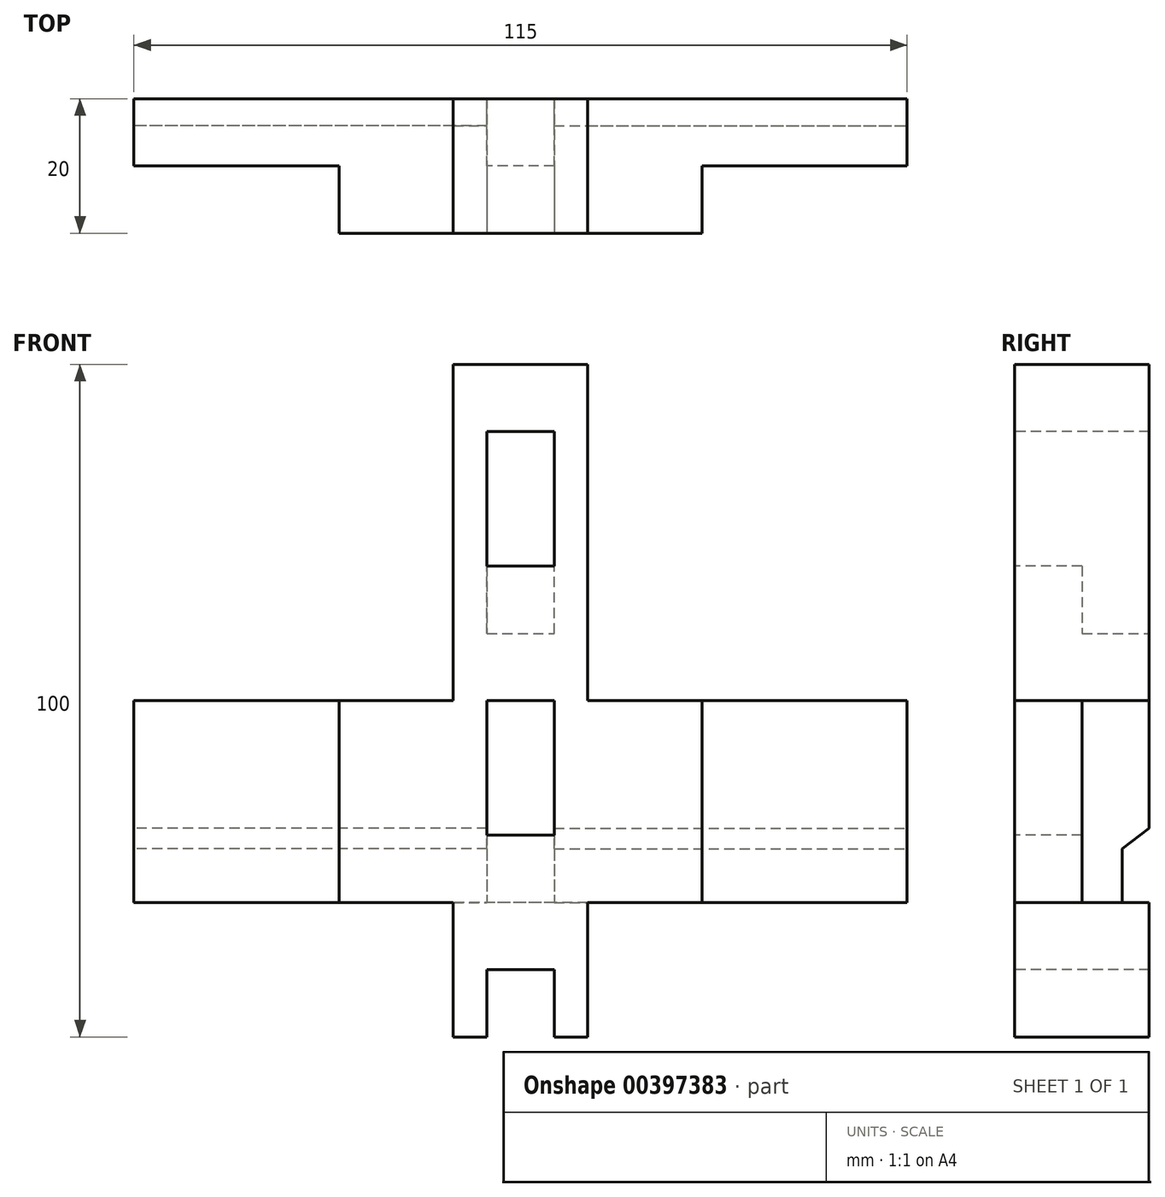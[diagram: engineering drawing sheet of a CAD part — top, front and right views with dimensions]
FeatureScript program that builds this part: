
annotation { "Feature Type Name" : "Feature", "Feature Type Description" : "" }
export const myFeature = defineFeature(function(context is Context, id is Id, definition is map)
    precondition{}
    {
        {
            var Q0;
            Q0=qCreatedBy(makeId("Front.planeOp"),FACE);
            var sketch = newSketch(context, id + "F0", { "sketchPlane" : qUnion([Q0])});
            skLineSegment(sketch, "E0", {"start": v(0, 0) * mm, "end": v(0, 100) * mm});
            skLineSegment(sketch, "E1", {"start": v(0, 100) * mm, "end": v(-10, 100) * mm});
            skLineSegment(sketch, "E2", {"start": v(-10, 100) * mm, "end": v(-10, 50) * mm});
            skLineSegment(sketch, "E3", {"start": v(-10, 50) * mm, "end": v(-57.5, 50) * mm});
            skLineSegment(sketch, "E4", {"start": v(-57.5, 50) * mm, "end": v(-57.5, 20) * mm});
            skLineSegment(sketch, "E5", {"start": v(-57.5, 20) * mm, "end": v(-10, 20) * mm});
            skLineSegment(sketch, "E6", {"start": v(-10, 20) * mm, "end": v(-10, 0) * mm});
            skLineSegment(sketch, "E7", {"start": v(-10, 0) * mm, "end": v(0, 0) * mm});
            skLineSegment(sketch, "E8.MirrorCS", {"start": v(10, 100) * mm, "end": v(10, 50) * mm});
            skLineSegment(sketch, "E9.MirrorCS", {"start": v(57.5, 50) * mm, "end": v(57.5, 20) * mm});
            skLineSegment(sketch, "E10.MirrorCS", {"start": v(57.5, 20) * mm, "end": v(10, 20) * mm});
            skLineSegment(sketch, "E11.MirrorCS", {"start": v(0, 100) * mm, "end": v(10, 100) * mm});
            skLineSegment(sketch, "E12.MirrorCS", {"start": v(10, 50) * mm, "end": v(57.5, 50) * mm});
            skLineSegment(sketch, "E13.MirrorCS", {"start": v(10, 20) * mm, "end": v(10, 0) * mm});
            skLineSegment(sketch, "E14.MirrorCS", {"start": v(10, 0) * mm, "end": v(0, 0) * mm});
            skSolve(sketch);
        }
        {
            var Q0;
            Q0 = qSketchRegion(id + "F0", true);
            extrude(context, id + "F1", {"entities" : qUnion([Q0]), "depth" : 20 * mm});
        }
        {
            var Q0;
            Q0=makeQuery(id+"F1.opExtrude","SWEPT_FACE",FACE,{"disambiguationData":[OSD([sQuery(id+"F0.wireOp",EDGE,"E5")])]});
            var sketch = newSketch(context, id + "F2", { "sketchPlane" : qUnion([Q0])});
            skLineSegment(sketch, "E15.bottom", {"start": v(-57.5, 20) * mm, "end": v(-27, 20) * mm});
            skLineSegment(sketch, "E15.top", {"start": v(-57.5, 10) * mm, "end": v(-27, 10) * mm});
            skLineSegment(sketch, "E15.left", {"start": v(-57.5, 20) * mm, "end": v(-57.5, 10) * mm});
            skLineSegment(sketch, "E15.right", {"start": v(-27, 20) * mm, "end": v(-27, 10) * mm});
            skSolve(sketch);
        }
        {
            var Q0;
            Q0=makeQuery(id+"F2.imprint","IMPRINT",FACE,{"disambiguationData":[TD([[makeQuery(id+"F2.imprint","IMPRINT",EDGE,{"derivedFrom":sQuery(id+"F2.wireOp",EDGE,"E15.bottom")}),-1.0]])]});
            extrude(context, id + "F3", {"entities" : qUnion([Q0]), "operationType" : NewBodyOperationType.REMOVE, "endBound" : BoundingType.UP_TO_NEXT, "oppositeDirection" : true, "depth" : 25.4 * mm});
        }
        {
            var Q0;
            Q0=makeQuery(id+"F1.opExtrude","SWEPT_FACE",FACE,{"disambiguationData":[OSD([sQuery(id+"F0.wireOp",EDGE,"E10.MirrorCS")])]});
            var sketch = newSketch(context, id + "F4", { "sketchPlane" : qUnion([Q0])});
            skLineSegment(sketch, "E16.bottom", {"start": v(57.5, 20) * mm, "end": v(27, 20) * mm});
            skLineSegment(sketch, "E16.top", {"start": v(57.5, 10) * mm, "end": v(27, 10) * mm});
            skLineSegment(sketch, "E16.left", {"start": v(57.5, 20) * mm, "end": v(57.5, 10) * mm});
            skLineSegment(sketch, "E16.right", {"start": v(27, 20) * mm, "end": v(27, 10) * mm});
            skSolve(sketch);
        }
        {
            var Q0;
            Q0=makeQuery(id+"F4.imprint","IMPRINT",FACE,{"disambiguationData":[TD([[makeQuery(id+"F4.imprint","IMPRINT",EDGE,{"derivedFrom":sQuery(id+"F4.wireOp",EDGE,"E16.bottom")}),1.0]])]});
            extrude(context, id + "F5", {"entities" : qUnion([Q0]), "operationType" : NewBodyOperationType.REMOVE, "endBound" : BoundingType.UP_TO_NEXT, "oppositeDirection" : true, "depth" : 25.4 * mm});
        }
        {
            var Q0;
            Q0=makeQuery(id+"F1.opExtrude","SWEPT_FACE",FACE,{"disambiguationData":[OSD([sQuery(id+"F0.wireOp",EDGE,"E4")])]});
            var sketch = newSketch(context, id + "F6", { "sketchPlane" : qUnion([Q0])});
            skLineSegment(sketch, "E17", {"start": v(0, 20) * mm, "end": v(4, 20) * mm});
            skLineSegment(sketch, "E18", {"start": v(4, 20) * mm, "end": v(4, 28) * mm});
            skLineSegment(sketch, "E19", {"start": v(0, 28) * mm, "end": v(0, 20) * mm});
            skLineSegment(sketch, "E20", {"start": v(0, 31) * mm, "end": v(0, 28) * mm});
            skLineSegment(sketch, "E21", {"start": v(0, 31) * mm, "end": v(4, 28) * mm});
            skSolve(sketch);
        }
        {
            var Q0;
            Q0=makeQuery(id+"F6.imprint","IMPRINT",FACE,{"disambiguationData":[TD([[makeQuery(id+"F6.imprint","IMPRINT",EDGE,{"derivedFrom":sQuery(id+"F6.wireOp",EDGE,"E17")}),-1.0]])]});
            var Q1;
            Q1=makeQuery(id+"F1.opExtrude","SWEPT_FACE",FACE,{"disambiguationData":[OSD([sQuery(id+"F0.wireOp",EDGE,"E6")])]});
            extrude(context, id + "F7", {"entities" : qUnion([Q0]), "operationType" : NewBodyOperationType.REMOVE, "endBound" : BoundingType.UP_TO_SURFACE, "oppositeDirection" : true, "endBoundEntityFace" : qUnion([Q1]), "depth" : 40 * mm});
        }
        {
            var Q0;
            Q0=makeQuery(id+"F1.opExtrude","CAP_FACE",FACE,{"disambiguationData":[OSD([sQuery(id+"F0.wireOp",EDGE,"E1"),sQuery(id+"F0.wireOp",EDGE,"E2"),sQuery(id+"F0.wireOp",EDGE,"E3"),sQuery(id+"F0.wireOp",EDGE,"E4"),sQuery(id+"F0.wireOp",EDGE,"E5"),sQuery(id+"F0.wireOp",EDGE,"E6"),sQuery(id+"F0.wireOp",EDGE,"E7"),sQuery(id+"F0.wireOp",EDGE,"E8.MirrorCS"),sQuery(id+"F0.wireOp",EDGE,"E9.MirrorCS"),sQuery(id+"F0.wireOp",EDGE,"E10.MirrorCS"),sQuery(id+"F0.wireOp",EDGE,"E11.MirrorCS"),sQuery(id+"F0.wireOp",EDGE,"E12.MirrorCS"),sQuery(id+"F0.wireOp",EDGE,"E13.MirrorCS"),sQuery(id+"F0.wireOp",EDGE,"E14.MirrorCS")])],"isStart":false});
            var sketch = newSketch(context, id + "F8", { "sketchPlane" : qUnion([Q0])});
            skLineSegment(sketch, "E22.bottom", {"start": v(-5, 90) * mm, "end": v(5, 90) * mm});
            skLineSegment(sketch, "E22.top", {"start": v(-5, 70) * mm, "end": v(5, 70) * mm});
            skLineSegment(sketch, "E22.left", {"start": v(-5, 90) * mm, "end": v(-5, 70) * mm});
            skLineSegment(sketch, "E22.right", {"start": v(5, 90) * mm, "end": v(5, 70) * mm});
            skLineSegment(sketch, "E23.bottom", {"start": v(-5, 50) * mm, "end": v(5, 50) * mm});
            skLineSegment(sketch, "E23.top", {"start": v(-5, 30) * mm, "end": v(5, 30) * mm});
            skLineSegment(sketch, "E23.left", {"start": v(-5, 50) * mm, "end": v(-5, 30) * mm});
            skLineSegment(sketch, "E23.right", {"start": v(5, 50) * mm, "end": v(5, 30) * mm});
            skLineSegment(sketch, "E24.bottom", {"start": v(5, 10) * mm, "end": v(-5, 10) * mm});
            skLineSegment(sketch, "E24.top", {"start": v(5, -10) * mm, "end": v(-5, -10) * mm});
            skLineSegment(sketch, "E24.left", {"start": v(5, 10) * mm, "end": v(5, -10) * mm});
            skLineSegment(sketch, "E24.right", {"start": v(-5, 10) * mm, "end": v(-5, -10) * mm});
            skSolve(sketch);
        }
        {
            var Q0;
            Q0=makeQuery(id+"F8.imprint","IMPRINT",FACE,{"disambiguationData":[TD([[makeQuery(id+"F8.imprint","IMPRINT",EDGE,{"derivedFrom":sQuery(id+"F8.wireOp",EDGE,"E22.bottom")}),-1.0]])]});
            var Q1;
            Q1=makeQuery(id+"F8.imprint","IMPRINT",FACE,{"disambiguationData":[TD([[makeQuery(id+"F8.imprint","IMPRINT",EDGE,{"derivedFrom":sQuery(id+"F8.wireOp",EDGE,"E23.bottom")}),-1.0]])]});
            var Q2;
            {var subQ0=sQuery(id+"F8.wireOp",EDGE,"E24.bottom");Q2=makeQuery(id+"F8.imprint","IMPRINT",FACE,{"disambiguationData":[TD([[makeQuery(id+"F8.imprint","IMPRINT",EDGE,{"derivedFrom":subQ0}),1.0]])]});}
            extrude(context, id + "F9", {"entities" : qUnion([Q0, Q1, Q2]), "operationType" : NewBodyOperationType.REMOVE, "endBound" : BoundingType.UP_TO_NEXT, "oppositeDirection" : true, "depth" : 25.4 * mm});
        }
        {
            var Q0;
            {var subQ0=sQuery(id+"F0.wireOp",EDGE,"E4");var subQ1=sQuery(id+"F0.wireOp",EDGE,"E3");var subQ2=sQuery(id+"F0.wireOp",EDGE,"E2");var subQ3=sQuery(id+"F0.wireOp",EDGE,"E11.MirrorCS");var subQ4=sQuery(id+"F0.wireOp",EDGE,"E1");var subQ5=sQuery(id+"F0.wireOp",EDGE,"E8.MirrorCS");var subQ6=sQuery(id+"F0.wireOp",EDGE,"E9.MirrorCS");var subQ7=sQuery(id+"F0.wireOp",EDGE,"E12.MirrorCS");Q0=makeQuery(id+"F7.boolean.opBoolean","SPLIT",FACE,{"disambiguationData":[TD([makeQuery(id+"F1.opExtrude","SWEPT_FACE",FACE,{"disambiguationData":[OSD([subQ2])]})])],"derivedFrom":makeQuery(id+"F1.opExtrude","CAP_FACE",FACE,{"disambiguationData":[OSD([subQ4,subQ2,subQ1,subQ0,sQuery(id+"F0.wireOp",EDGE,"E5"),sQuery(id+"F0.wireOp",EDGE,"E6"),sQuery(id+"F0.wireOp",EDGE,"E7"),subQ5,subQ6,sQuery(id+"F0.wireOp",EDGE,"E10.MirrorCS"),subQ3,subQ7,sQuery(id+"F0.wireOp",EDGE,"E13.MirrorCS"),sQuery(id+"F0.wireOp",EDGE,"E14.MirrorCS")])],"isStart":true})});}
            var sketch = newSketch(context, id + "F10", { "sketchPlane" : qUnion([Q0])});
            skLineSegment(sketch, "E25", {"start": v(-5, 70) * mm, "end": v(5, 70) * mm});
            skLineSegment(sketch, "E26", {"start": v(5, 70) * mm, "end": v(5, 60) * mm});
            skLineSegment(sketch, "E27", {"start": v(5, 60) * mm, "end": v(-5, 60) * mm});
            skLineSegment(sketch, "E28", {"start": v(-5, 60) * mm, "end": v(-5, 70) * mm});
            skLineSegment(sketch, "E29.bottom", {"start": v(-5, 30) * mm, "end": v(5, 30) * mm});
            skLineSegment(sketch, "E29.top", {"start": v(-5, 20) * mm, "end": v(5, 20) * mm});
            skLineSegment(sketch, "E29.left", {"start": v(-5, 30) * mm, "end": v(-5, 20) * mm});
            skLineSegment(sketch, "E29.right", {"start": v(5, 30) * mm, "end": v(5, 20) * mm});
            skSolve(sketch);
        }
        {
            var Q0;
            Q0=makeQuery(id+"F10.imprint","IMPRINT",FACE,{"disambiguationData":[TD([[makeQuery(id+"F10.imprint","IMPRINT",EDGE,{"derivedFrom":sQuery(id+"F10.wireOp",EDGE,"E25")}),-1.0]])]});
            var Q1;
            Q1=makeQuery(id+"F10.imprint","IMPRINT",FACE,{"disambiguationData":[TD([[makeQuery(id+"F10.imprint","IMPRINT",EDGE,{"derivedFrom":sQuery(id+"F10.wireOp",EDGE,"E29.bottom")}),-1.0]])]});
            extrude(context, id + "F11", {"entities" : qUnion([Q0, Q1]), "operationType" : NewBodyOperationType.REMOVE, "oppositeDirection" : true, "depth" : 10 * mm});
        }
        {
            var Q0;
            Q0=makeQuery(id+"F1.opExtrude","SWEPT_FACE",FACE,{"disambiguationData":[OSD([sQuery(id+"F0.wireOp",EDGE,"E9.MirrorCS")])]});
            var sketch = newSketch(context, id + "F12", { "sketchPlane" : qUnion([Q0])});
            skLineSegment(sketch, "E30", {"start": v(0, 20) * mm, "end": v(4, 20) * mm});
            skLineSegment(sketch, "E31", {"start": v(4, 20) * mm, "end": v(4, 28) * mm});
            skLineSegment(sketch, "E32", {"start": v(0, 28) * mm, "end": v(0, 20) * mm});
            skLineSegment(sketch, "E33", {"start": v(0, 31) * mm, "end": v(0, 28) * mm});
            skLineSegment(sketch, "E34", {"start": v(0, 31) * mm, "end": v(4, 28) * mm});
            skLineSegment(sketch, "E35.MirrorCS", {"start": v(0, 20) * mm, "end": v(-4, 20) * mm});
            skLineSegment(sketch, "E36.MirrorCS", {"start": v(0, 31) * mm, "end": v(-4, 28) * mm});
            skLineSegment(sketch, "E37.MirrorCS", {"start": v(-4, 20) * mm, "end": v(-4, 28) * mm});
            skSolve(sketch);
        }
        {
            var Q0;
            Q0=makeQuery(id+"F12.imprint","IMPRINT",FACE,{"disambiguationData":[TD([[makeQuery(id+"F12.imprint","IMPRINT",EDGE,{"derivedFrom":sQuery(id+"F12.wireOp",EDGE,"E35.MirrorCS")}),1.0]])]});
            extrude(context, id + "F13", {"entities" : qUnion([Q0]), "operationType" : NewBodyOperationType.REMOVE, "oppositeDirection" : true, "depth" : 150 * mm});
        }
    });
